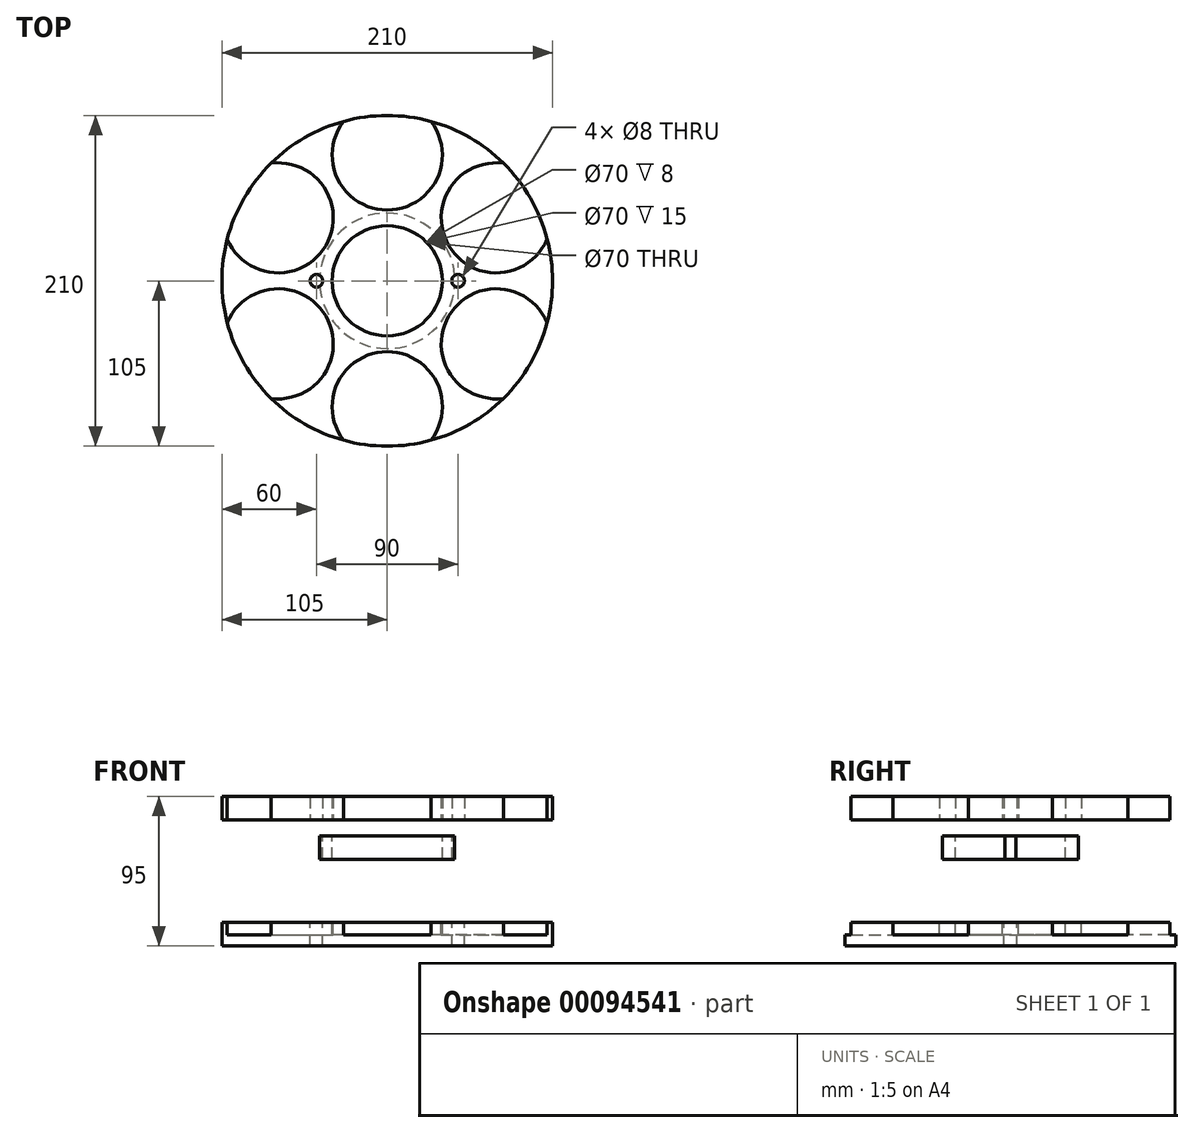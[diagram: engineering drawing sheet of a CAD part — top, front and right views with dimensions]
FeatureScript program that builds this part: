
annotation { "Feature Type Name" : "Feature", "Feature Type Description" : "" }
export const myFeature = defineFeature(function(context is Context, id is Id, definition is map)
    precondition{}
    {
        {
            var Q0;
            Q0=qCreatedBy(makeId("Top.planeOp"),FACE);
            var sketch = newSketch(context, id + "F0", { "sketchPlane" : qUnion([Q0])});
            skLineSegment(sketch, "E0", {"start": v(0, 0) * mm, "end": v(0, -80) * mm, "construction": true});
            skCircle(sketch, "E1", {"center": v(0, -80) * mm, "radius": 35 * mm});
            skCircle(sketch, "E2.1.0", {"center": v(69.28, -40) * mm, "radius": 35 * mm});
            skCircle(sketch, "E2.2.0", {"center": v(69.28, 40) * mm, "radius": 35 * mm});
            skCircle(sketch, "E2.3.0", {"center": v(0, 80) * mm, "radius": 35 * mm});
            skCircle(sketch, "E2.4.0", {"center": v(-69.28, 40) * mm, "radius": 35 * mm});
            skCircle(sketch, "E2.5.0", {"center": v(-69.28, -40) * mm, "radius": 35 * mm});
            skPoint(sketch, "E2.center", {"position": v(0, 0) * mm});
            skCircle(sketch, "E3", {"center": v(0, 0) * mm, "radius": 105 * mm});
            skLineSegment(sketch, "E4", {"start": v(-45, 0) * mm, "end": v(0, 0) * mm, "construction": true});
            skCircle(sketch, "E5", {"center": v(-45, 0) * mm, "radius": 4 * mm});
            skCircle(sketch, "E6", {"center": v(0, 0) * mm, "radius": 35 * mm});
            skCircle(sketch, "E7.MirrorC", {"center": v(45, 0) * mm, "radius": 4 * mm});
            skCircle(sketch, "E8", {"center": v(0, 0) * mm, "radius": 43.03 * mm});
            skSolve(sketch);
        }
        {
            var Q0;
            Q0=makeQuery(id+"F0.imprint","IMPRINT",FACE,{"disambiguationData":[TD([[makeQuery(id+"F0.imprint","IMPRINT",EDGE,{"derivedFrom":sQuery(id+"F0.wireOp",EDGE,"E5")}),-1.0]])]});
            var Q1;
            {var subQ0=sQuery(id+"F0.wireOp",EDGE,"E3");var subQ1=sQuery(id+"F0.wireOp",EDGE,"E1");var subQ2=makeQuery(id+"F0.imprint","INTERSECT",VERTEX,{"disambiguationData":[OD(0.0)],"derivedFrom":[subQ1,subQ0]});Q1=makeQuery(id+"F0.imprint","IMPRINT",FACE,{"disambiguationData":[TD([[makeQuery(id+"F0.imprint","IMPRINT",EDGE,{"disambiguationData":[TD([[subQ2,1.0]])],"derivedFrom":subQ1}),-1.0]])]});}
            extrude(context, id + "F1", {"entities" : qUnion([Q0, Q1]), "depth" : 15 * mm});
        }
        {
            var Q0;
            Q0=makeQuery(id+"F0.imprint","IMPRINT",FACE,{"disambiguationData":[TD([[makeQuery(id+"F0.imprint","IMPRINT",EDGE,{"derivedFrom":sQuery(id+"F0.wireOp",EDGE,"E5")}),-1.0]])]});
            var Q1;
            {var subQ0=sQuery(id+"F0.wireOp",EDGE,"E3");var subQ1=sQuery(id+"F0.wireOp",EDGE,"E2.4.0");var subQ2=makeQuery(id+"F0.imprint","INTERSECT",VERTEX,{"disambiguationData":[OD(0.0)],"derivedFrom":[subQ1,subQ0]});Q1=makeQuery(id+"F0.imprint","IMPRINT",FACE,{"disambiguationData":[TD([[makeQuery(id+"F0.imprint","IMPRINT",EDGE,{"disambiguationData":[TD([[subQ2,1.0]])],"derivedFrom":subQ1}),1.0]])]});}
            var Q2;
            {var subQ0=sQuery(id+"F0.wireOp",EDGE,"E3");var subQ1=sQuery(id+"F0.wireOp",EDGE,"E2.3.0");var subQ2=makeQuery(id+"F0.imprint","INTERSECT",VERTEX,{"disambiguationData":[OD(0.0)],"derivedFrom":[subQ1,subQ0]});Q2=makeQuery(id+"F0.imprint","IMPRINT",FACE,{"disambiguationData":[TD([[makeQuery(id+"F0.imprint","IMPRINT",EDGE,{"disambiguationData":[TD([[subQ2,1.0]])],"derivedFrom":subQ1}),1.0]])]});}
            var Q3;
            {var subQ0=sQuery(id+"F0.wireOp",EDGE,"E3");var subQ1=sQuery(id+"F0.wireOp",EDGE,"E2.2.0");var subQ2=makeQuery(id+"F0.imprint","INTERSECT",VERTEX,{"disambiguationData":[OD(0.0)],"derivedFrom":[subQ1,subQ0]});Q3=makeQuery(id+"F0.imprint","IMPRINT",FACE,{"disambiguationData":[TD([[makeQuery(id+"F0.imprint","IMPRINT",EDGE,{"disambiguationData":[TD([[subQ2,-1.0]])],"derivedFrom":subQ1}),1.0]])]});}
            var Q4;
            {var subQ0=sQuery(id+"F0.wireOp",EDGE,"E3");var subQ1=sQuery(id+"F0.wireOp",EDGE,"E2.1.0");var subQ2=makeQuery(id+"F0.imprint","INTERSECT",VERTEX,{"disambiguationData":[OD(0.0)],"derivedFrom":[subQ1,subQ0]});Q4=makeQuery(id+"F0.imprint","IMPRINT",FACE,{"disambiguationData":[TD([[makeQuery(id+"F0.imprint","IMPRINT",EDGE,{"disambiguationData":[TD([[subQ2,1.0]])],"derivedFrom":subQ1}),1.0]])]});}
            var Q5;
            Q5=makeQuery(id+"F0.imprint","IMPRINT",FACE,{"disambiguationData":[TD([[makeQuery(id+"F0.imprint","IMPRINT",EDGE,{"derivedFrom":sQuery(id+"F0.wireOp",EDGE,"E6")}),1.0]])]});
            var Q6;
            {var subQ0=sQuery(id+"F0.wireOp",EDGE,"E3");var subQ1=sQuery(id+"F0.wireOp",EDGE,"E1");var subQ2=makeQuery(id+"F0.imprint","INTERSECT",VERTEX,{"disambiguationData":[OD(0.0)],"derivedFrom":[subQ1,subQ0]});Q6=makeQuery(id+"F0.imprint","IMPRINT",FACE,{"disambiguationData":[TD([[makeQuery(id+"F0.imprint","IMPRINT",EDGE,{"disambiguationData":[TD([[subQ2,1.0]])],"derivedFrom":subQ1}),1.0]])]});}
            var Q7;
            {var subQ0=sQuery(id+"F0.wireOp",EDGE,"E3");var subQ1=sQuery(id+"F0.wireOp",EDGE,"E2.5.0");var subQ2=makeQuery(id+"F0.imprint","INTERSECT",VERTEX,{"disambiguationData":[OD(0.0)],"derivedFrom":[subQ1,subQ0]});Q7=makeQuery(id+"F0.imprint","IMPRINT",FACE,{"disambiguationData":[TD([[makeQuery(id+"F0.imprint","IMPRINT",EDGE,{"disambiguationData":[TD([[subQ2,1.0]])],"derivedFrom":subQ1}),1.0]])]});}
            var Q8;
            {var subQ0=sQuery(id+"F0.wireOp",EDGE,"E3");var subQ1=sQuery(id+"F0.wireOp",EDGE,"E1");var subQ2=makeQuery(id+"F0.imprint","INTERSECT",VERTEX,{"disambiguationData":[OD(0.0)],"derivedFrom":[subQ1,subQ0]});Q8=makeQuery(id+"F0.imprint","IMPRINT",FACE,{"disambiguationData":[TD([[makeQuery(id+"F0.imprint","IMPRINT",EDGE,{"disambiguationData":[TD([[subQ2,1.0]])],"derivedFrom":subQ1}),-1.0]])]});}
            extrude(context, id + "F2", {"entities" : qUnion([Q0, Q1, Q2, Q3, Q4, Q5, Q6, Q7, Q8]), "oppositeDirection" : true, "depth" : 80 * mm, "hasSecondDirection" : true, "secondDirectionOppositeDirection" : true, "secondDirectionDepth" : 65 * mm});
        }
        {
            var Q0;
            {var subQ0=sQuery(id+"F0.wireOp",EDGE,"E3");var subQ1=sQuery(id+"F0.wireOp",EDGE,"E2.5.0");var subQ2=makeQuery(id+"F0.imprint","INTERSECT",VERTEX,{"disambiguationData":[OD(0.0)],"derivedFrom":[subQ1,subQ0]});Q0=makeQuery(id+"F0.imprint","IMPRINT",FACE,{"disambiguationData":[TD([[makeQuery(id+"F0.imprint","IMPRINT",EDGE,{"disambiguationData":[TD([[subQ2,1.0]])],"derivedFrom":subQ1}),1.0]])]});}
            var Q1;
            {var subQ0=sQuery(id+"F0.wireOp",EDGE,"E3");var subQ1=sQuery(id+"F0.wireOp",EDGE,"E2.4.0");var subQ2=makeQuery(id+"F0.imprint","INTERSECT",VERTEX,{"disambiguationData":[OD(0.0)],"derivedFrom":[subQ1,subQ0]});Q1=makeQuery(id+"F0.imprint","IMPRINT",FACE,{"disambiguationData":[TD([[makeQuery(id+"F0.imprint","IMPRINT",EDGE,{"disambiguationData":[TD([[subQ2,1.0]])],"derivedFrom":subQ1}),1.0]])]});}
            var Q2;
            {var subQ0=sQuery(id+"F0.wireOp",EDGE,"E3");var subQ1=sQuery(id+"F0.wireOp",EDGE,"E2.3.0");var subQ2=makeQuery(id+"F0.imprint","INTERSECT",VERTEX,{"disambiguationData":[OD(0.0)],"derivedFrom":[subQ1,subQ0]});Q2=makeQuery(id+"F0.imprint","IMPRINT",FACE,{"disambiguationData":[TD([[makeQuery(id+"F0.imprint","IMPRINT",EDGE,{"disambiguationData":[TD([[subQ2,1.0]])],"derivedFrom":subQ1}),1.0]])]});}
            var Q3;
            {var subQ0=sQuery(id+"F0.wireOp",EDGE,"E3");var subQ1=sQuery(id+"F0.wireOp",EDGE,"E2.2.0");var subQ2=makeQuery(id+"F0.imprint","INTERSECT",VERTEX,{"disambiguationData":[OD(0.0)],"derivedFrom":[subQ1,subQ0]});Q3=makeQuery(id+"F0.imprint","IMPRINT",FACE,{"disambiguationData":[TD([[makeQuery(id+"F0.imprint","IMPRINT",EDGE,{"disambiguationData":[TD([[subQ2,-1.0]])],"derivedFrom":subQ1}),1.0]])]});}
            var Q4;
            {var subQ0=sQuery(id+"F0.wireOp",EDGE,"E3");var subQ1=sQuery(id+"F0.wireOp",EDGE,"E1");var subQ2=makeQuery(id+"F0.imprint","INTERSECT",VERTEX,{"disambiguationData":[OD(0.0)],"derivedFrom":[subQ1,subQ0]});Q4=makeQuery(id+"F0.imprint","IMPRINT",FACE,{"disambiguationData":[TD([[makeQuery(id+"F0.imprint","IMPRINT",EDGE,{"disambiguationData":[TD([[subQ2,1.0]])],"derivedFrom":subQ1}),1.0]])]});}
            var Q5;
            {var subQ0=sQuery(id+"F0.wireOp",EDGE,"E3");var subQ1=sQuery(id+"F0.wireOp",EDGE,"E2.1.0");var subQ2=makeQuery(id+"F0.imprint","INTERSECT",VERTEX,{"disambiguationData":[OD(0.0)],"derivedFrom":[subQ1,subQ0]});Q5=makeQuery(id+"F0.imprint","IMPRINT",FACE,{"disambiguationData":[TD([[makeQuery(id+"F0.imprint","IMPRINT",EDGE,{"disambiguationData":[TD([[subQ2,1.0]])],"derivedFrom":subQ1}),1.0]])]});}
            var Q6;
            Q6=makeQuery(id+"F0.imprint","IMPRINT",FACE,{"disambiguationData":[TD([[makeQuery(id+"F0.imprint","IMPRINT",EDGE,{"derivedFrom":sQuery(id+"F0.wireOp",EDGE,"E6")}),1.0]])]});
            extrude(context, id + "F3", {"entities" : qUnion([Q0, Q1, Q2, Q3, Q4, Q5, Q6]), "operationType" : NewBodyOperationType.REMOVE, "oppositeDirection" : true, "depth" : 73 * mm});
        }
        {
            var Q0;
            Q0=makeQuery(id+"F0.imprint","IMPRINT",FACE,{"disambiguationData":[TD([[makeQuery(id+"F0.imprint","IMPRINT",EDGE,{"derivedFrom":sQuery(id+"F0.wireOp",EDGE,"E6")}),-1.0]])]});
            extrude(context, id + "F4", {"entities" : qUnion([Q0]), "oppositeDirection" : true, "depth" : 25 * mm, "hasSecondDirection" : true, "secondDirectionOppositeDirection" : true, "secondDirectionDepth" : 10 * mm});
        }
    });
